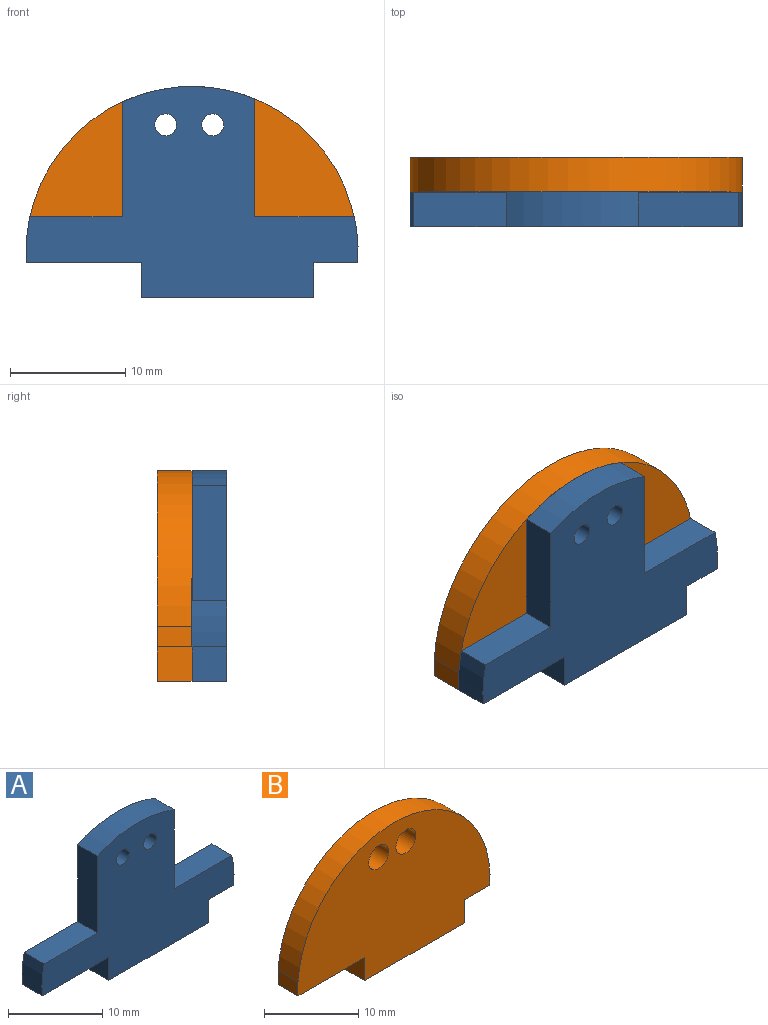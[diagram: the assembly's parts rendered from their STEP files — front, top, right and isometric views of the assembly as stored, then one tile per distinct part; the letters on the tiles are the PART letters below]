
ASSEMBLY  parts=2 mates=1
PART A: 17 faces, bbox 28.9x3x18.3 mm
  f0: plane 3x3mm, normal (-1,0,0), area 9mm2, adj f1,f14,f15,f16
  f1: plane 15x3mm, normal (0,0,-1), area 45mm2, adj f0,f2,f15,f16
  f2: plane 3x3mm, normal (1,0,0), area 9mm2, adj f1,f3,f15,f16
  f3: plane 3.81x3mm, normal (0,0,-1), area 11.4mm2, adj f2,f4,f15,f16
  f4: extruded ~3x1.39mm, area 4.2mm2, adj f3,f5,f15,f16
  f5: cylinder r=14.43mm len=3mm, axis (0,1,0), area 7.9mm2, adj f4,f6,f15,f16
  f6: plane 8.64x3mm, normal (0,0,1), area 25.9mm2, adj f5,f7,f15,f16
  f7: plane 10.27x3mm, normal (1,0,0), area 30.8mm2, adj f6,f8,f15,f16
  f8: cylinder r=14.43mm len=11.53mm, axis (0,1,0), area 35.6mm2, adj f7,f9,f15,f16
  f9: plane 10x3mm, normal (-1,0,0), area 30mm2, adj f8,f10,f15,f16
  f10: plane 8.02x3mm, normal (0,0,1), area 24.1mm2, adj f9,f11,f15,f16
  f11: cylinder r=14.43mm len=4mm, axis (0,1,0), area 12.1mm2, adj f10,f14,f15,f16
  f12: cylinder r=0.95mm len=3mm, axis (0,1,0), area 17.9mm2, adj f15,f16
  f13: cylinder r=0.95mm len=3mm, axis (0,1,0), area 17.9mm2, adj f15,f16
  f14: plane 10x3mm, normal (0,0,-1), area 30mm2, adj f0,f11,f15,f16
  f15: plane 28.85x18.34mm, normal (0,-1,0), area 280.2mm2, adj f0,f1,f2,f3,f4,f5,f6,f7
  f16: plane 28.85x18.34mm, normal (0,1,0), area 280.2mm2, adj f0,f1,f2,f3,f4,f5,f6,f7
PART B: 12 faces, bbox 28.8x3x18.3 mm
  f0: plane 3x1.81mm, normal (-1,0,0), area 5.4mm2, adj f1,f9,f10,f11
  f1: plane 10x3mm, normal (0,0,-1), area 30mm2, adj f0,f2,f10,f11
  f2: plane 3x3mm, normal (-1,0,0), area 9mm2, adj f1,f3,f10,f11
  f3: plane 15x3mm, normal (0,0,-1), area 45mm2, adj f2,f4,f10,f11
  f4: plane 3x3mm, normal (1,0,0), area 9mm2, adj f3,f5,f10,f11
  f5: plane 3.81x3mm, normal (0,0,-1), area 11.4mm2, adj f4,f6,f10,f11
  f6: extruded ~3x1.39mm, area 4.2mm2, adj f5,f9,f10,f11
  f7: cylinder r=1.5mm len=3mm, axis (0,1,0), area 28.3mm2, adj f10,f11
  f8: cylinder r=1.5mm len=3mm, axis (0,1,0), area 28.3mm2, adj f10,f11
  f9: cylinder r=14.43mm len=28.83mm, axis (0,1,0), area 131.9mm2, adj f0,f6,f10,f11
  f10: plane 28.83x18.34mm, normal (0,-1,0), area 384.1mm2, adj f0,f1,f2,f3,f4,f5,f6,f7
  f11: plane 28.83x18.34mm, normal (0,1,0), area 384.1mm2, adj f0,f1,f2,f3,f4,f5,f6,f7
PLACE A t=(-12.26,-10.6,-3.02)mm
PLACE B t=(-12.26,-7.6,-3.02)mm
MATE fastened B.f10 <-> A.f16  axis (0,-1,0) through (-12.26,-10.6,-14.02)mm
